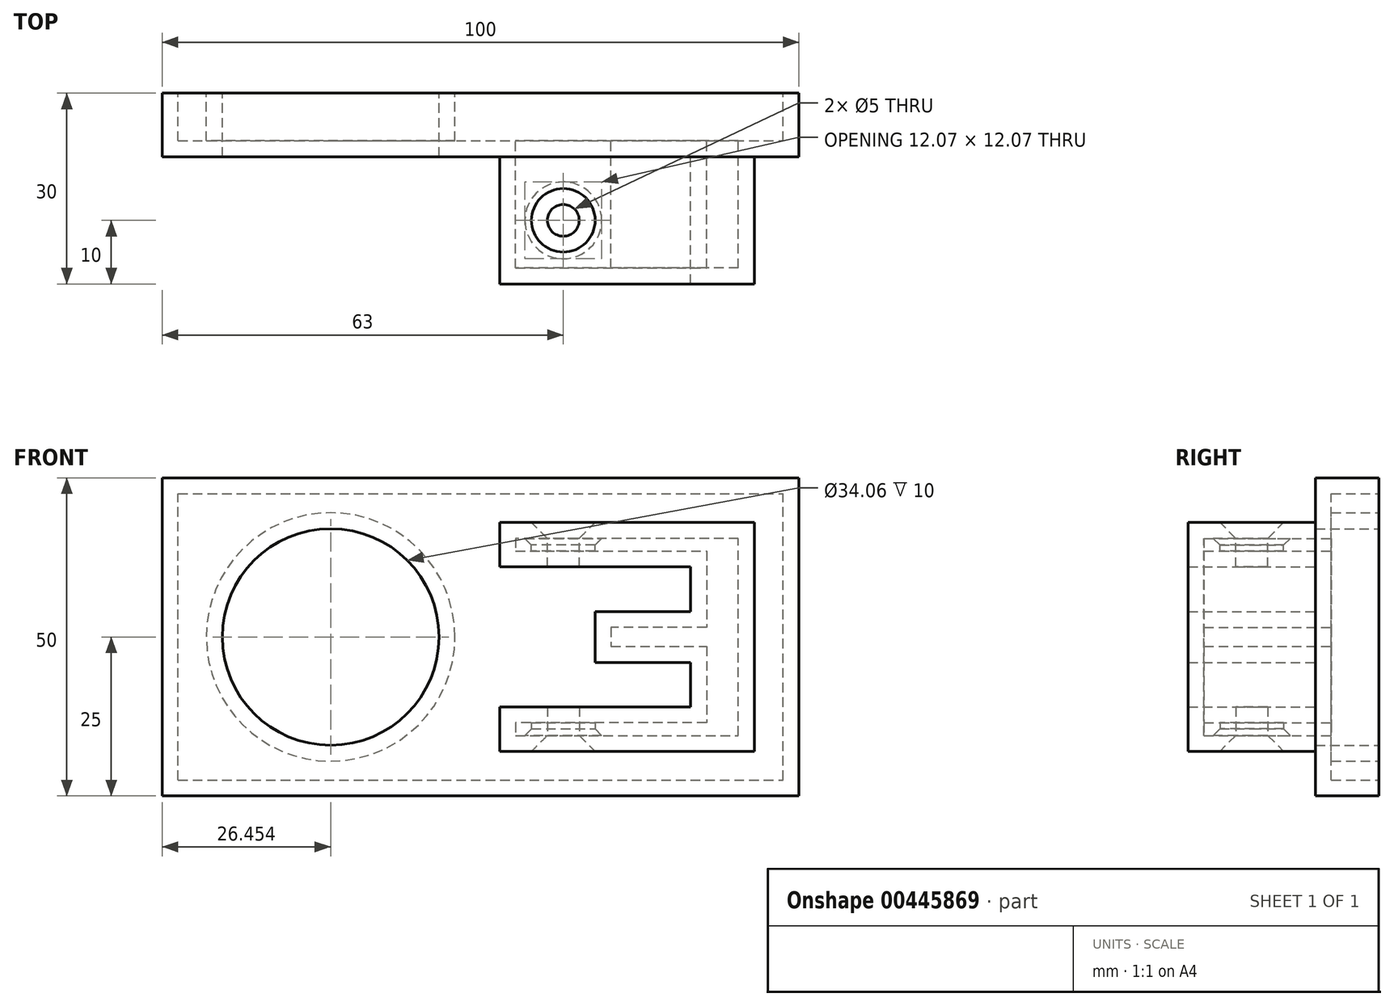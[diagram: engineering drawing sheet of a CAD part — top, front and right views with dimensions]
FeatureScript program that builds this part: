
annotation { "Feature Type Name" : "Feature", "Feature Type Description" : "" }
export const myFeature = defineFeature(function(context is Context, id is Id, definition is map)
    precondition{}
    {
        {
            var Q0;
            Q0=qCreatedBy(makeId("Front.planeOp"),FACE);
            var sketch = newSketch(context, id + "F0", { "sketchPlane" : qUnion([Q0])});
            skLineSegment(sketch, "E0.bottom", {"start": v(0, 0) * mm, "end": v(100, 0) * mm});
            skLineSegment(sketch, "E0.top", {"start": v(0, 50) * mm, "end": v(100, 50) * mm});
            skLineSegment(sketch, "E0.left", {"start": v(0, 0) * mm, "end": v(0, 50) * mm});
            skLineSegment(sketch, "E0.right", {"start": v(100, 0) * mm, "end": v(100, 50) * mm});
            skCircle(sketch, "E1", {"center": v(26.45, 25) * mm, "radius": 17.03 * mm});
            skLineSegment(sketch, "E2", {"start": v(0, 25) * mm, "end": v(100, 25) * mm, "construction": true});
            skLineSegment(sketch, "E3", {"start": v(50, 50) * mm, "end": v(50, 0) * mm, "construction": true});
            skSolve(sketch);
        }
        {
            var Q0;
            Q0=makeQuery(id+"F0.imprint","IMPRINT",FACE,{"disambiguationData":[TD([[makeQuery(id+"F0.imprint","IMPRINT",EDGE,{"derivedFrom":sQuery(id+"F0.wireOp",EDGE,"E0.bottom")}),1.0]])]});
            extrude(context, id + "F1", {"entities" : qUnion([Q0]), "depth" : 10 * mm});
        }
        {
            var Q0;
            Q0=makeQuery(id+"F1.opExtrude","CAP_FACE",FACE,{"disambiguationData":[OSD([sQuery(id+"F0.wireOp",EDGE,"E0.bottom"),sQuery(id+"F0.wireOp",EDGE,"E0.top"),sQuery(id+"F0.wireOp",EDGE,"E0.left"),sQuery(id+"F0.wireOp",EDGE,"E0.right"),sQuery(id+"F0.wireOp",EDGE,"E1")])],"isStart":false});
            var sketch = newSketch(context, id + "F2", { "sketchPlane" : qUnion([Q0])});
            skLineSegment(sketch, "E4", {"start": v(53, 43) * mm, "end": v(53, 36) * mm});
            skLineSegment(sketch, "E5", {"start": v(53, 36) * mm, "end": v(83, 36) * mm});
            skLineSegment(sketch, "E6", {"start": v(83, 36) * mm, "end": v(83, 29) * mm});
            skLineSegment(sketch, "E7", {"start": v(83, 29) * mm, "end": v(68, 29) * mm});
            skLineSegment(sketch, "E8", {"start": v(68, 29) * mm, "end": v(68, 21) * mm});
            skLineSegment(sketch, "E9", {"start": v(68, 21) * mm, "end": v(83, 21) * mm});
            skLineSegment(sketch, "E10", {"start": v(83, 21) * mm, "end": v(83, 14) * mm});
            skLineSegment(sketch, "E11", {"start": v(83, 14) * mm, "end": v(53, 14) * mm});
            skLineSegment(sketch, "E12", {"start": v(53, 14) * mm, "end": v(53, 7) * mm});
            skLineSegment(sketch, "E13", {"start": v(53, 7) * mm, "end": v(93, 7) * mm});
            skLineSegment(sketch, "E14", {"start": v(93, 7) * mm, "end": v(93, 43) * mm});
            skLineSegment(sketch, "E15", {"start": v(93, 43) * mm, "end": v(53, 43) * mm});
            skSolve(sketch);
        }
        {
            var Q0;
            Q0 = qSketchRegion(id + "F2", true);
            extrude(context, id + "F3", {"entities" : qUnion([Q0]), "operationType" : NewBodyOperationType.ADD, "depth" : 20 * mm});
        }
        {
            var Q0;
            Q0=makeQuery(id+"F3.opExtrude","SWEPT_FACE",FACE,{"disambiguationData":[OSD([sQuery(id+"F2.wireOp",EDGE,"E13")])]});
            var sketch = newSketch(context, id + "F4", { "sketchPlane" : qUnion([Q0])});
            skLineSegment(sketch, "E16", {"start": v(53, 20) * mm, "end": v(93, 20) * mm, "construction": true});
            skLineSegment(sketch, "E17", {"start": v(63, 30) * mm, "end": v(63, 10) * mm, "construction": true});
            skPoint(sketch, "E18", {"position": v(63, 20) * mm});
            skSolve(sketch);
        }
        {
            var Q0;
            Q0=sQuery(id+"F4.wireOp",VERTEX,"E18");
            var Q1;
            Q1=makeQuery(id+"F1.opExtrude","SWEPT_BODY",BODY,{"disambiguationData":[OSD([sQuery(id+"F0.wireOp",EDGE,"E0.bottom"),sQuery(id+"F0.wireOp",EDGE,"E0.top"),sQuery(id+"F0.wireOp",EDGE,"E0.left"),sQuery(id+"F0.wireOp",EDGE,"E0.right"),sQuery(id+"F0.wireOp",EDGE,"E1")])]});
            hole(context, id + "F5", {"style" : HoleStyle.C_SINK, "endStyle" : HoleEndStyle.BLIND, "holeDiameter" : 5 * mm, "cSinkDiameter" : 10 * mm, "cSinkAngle" : 90 * degree, "holeDepth" : 12 * mm, "isTappedThrough" : true, "tappedDepth" : 12 * mm, "tapClearance" : 3, "locations" : qUnion([Q0]), "scope" : qUnion([Q1])});
        }
        {
            var Q0;
            Q0=makeQuery(id+"F3.opExtrude","SWEPT_FACE",FACE,{"disambiguationData":[OSD([sQuery(id+"F2.wireOp",EDGE,"E15")])]});
            var sketch = newSketch(context, id + "F6", { "sketchPlane" : qUnion([Q0])});
            skLineSegment(sketch, "E19.0", {"start": v(53, -20) * mm, "end": v(93, -20) * mm, "construction": true});
            skLineSegment(sketch, "E20.0", {"start": v(63, -30) * mm, "end": v(63, -10) * mm, "construction": true});
            skPoint(sketch, "E21", {"position": v(63, -20) * mm});
            skSolve(sketch);
        }
        {
            var Q0;
            Q0=sQuery(id+"F6.wireOp",VERTEX,"E21");
            var Q1;
            Q1=makeQuery(id+"F1.opExtrude","SWEPT_BODY",BODY,{"disambiguationData":[OSD([sQuery(id+"F0.wireOp",EDGE,"E0.bottom"),sQuery(id+"F0.wireOp",EDGE,"E0.top"),sQuery(id+"F0.wireOp",EDGE,"E0.left"),sQuery(id+"F0.wireOp",EDGE,"E0.right"),sQuery(id+"F0.wireOp",EDGE,"E1")])]});
            hole(context, id + "F7", {"style" : HoleStyle.C_SINK, "endStyle" : HoleEndStyle.THROUGH, "holeDiameter" : 5 * mm, "cSinkDiameter" : 10 * mm, "cSinkAngle" : 90 * degree, "isTappedThrough" : true, "tappedDepth" : 12 * mm, "tapClearance" : 3, "locations" : qUnion([Q0]), "scope" : qUnion([Q1])});
        }
        {
            var Q0;
            Q0=makeQuery(id+"F1.opExtrude","CAP_FACE",FACE,{"disambiguationData":[OSD([sQuery(id+"F0.wireOp",EDGE,"E0.bottom"),sQuery(id+"F0.wireOp",EDGE,"E0.top"),sQuery(id+"F0.wireOp",EDGE,"E0.left"),sQuery(id+"F0.wireOp",EDGE,"E0.right"),sQuery(id+"F0.wireOp",EDGE,"E1")])],"isStart":true});
            shell(context, id + "F8", {"entities" : qUnion([Q0]), "thickness" : 2.5 * mm});
        }
    });
